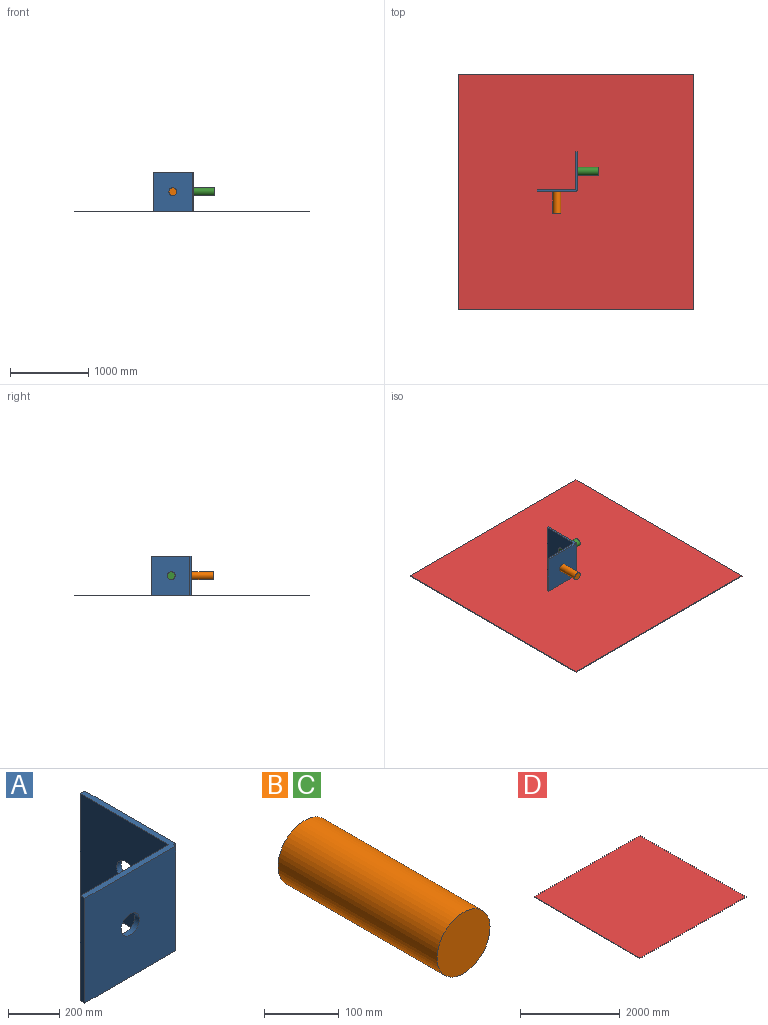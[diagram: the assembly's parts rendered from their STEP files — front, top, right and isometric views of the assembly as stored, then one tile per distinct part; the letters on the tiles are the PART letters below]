
ASSEMBLY  parts=4 mates=3
PART A: 12 faces, bbox 512.5x512.5x500 mm
  f0: plane 500x487.5mm, normal (0,1,0), area 235896mm2, adj f1,f3,f4,f5,f8
  f1: plane 512.5x512.5mm, normal (0,0,-1), area 24843.8mm2, adj f0,f2,f5,f6,f7,f8,f9,f11
  f2: plane 500x12.5mm, normal (1,0,0), area 6250mm2, adj f1,f3,f6,f7
  f3: plane 512.5x512.5mm, normal (0,0,1), area 24843.8mm2, adj f0,f2,f5,f6,f7,f8,f9,f11
  f4: cylinder r=50mm len=100mm, axis (0,1,0), area 7854mm2, adj f0,f6
  f5: plane 500x25mm, normal (-1,0,0), area 12500mm2, adj f0,f1,f3,f6
  f6: plane 500x500mm, normal (0,-1,0), area 242146mm2, adj f1,f2,f3,f4,f5
  f7: plane 500x12.5mm, normal (0,-1,0), area 6250mm2, adj f1,f2,f3,f11
  f8: plane 500x487.5mm, normal (-1,0,0), area 235896mm2, adj f0,f1,f3,f9,f10
  f9: plane 500x25mm, normal (0,1,0), area 12500mm2, adj f1,f3,f8,f11
  f10: cylinder r=50mm len=100mm, axis (-1,0,0), area 7854mm2, adj f8,f11
  f11: plane 500x500mm, normal (1,0,0), area 242146mm2, adj f1,f3,f7,f9,f10
PART B: 3 faces, bbox 100x300x100 mm
  f0: cylinder r=50mm len=300mm, axis (0,1,0), area 94247.8mm2, adj f1,f2
  f1: plane 100x100mm, normal (0,-1,0), area 7854mm2, adj f0
  f2: plane 100x100mm, normal (0,1,0), area 7854mm2, adj f0
PART C: same geometry as B
PART D: 6 faces, bbox 3000x3000x10 mm
  f0: plane 3000x10mm, normal (0,1,0), area 30000mm2, adj f1,f3,f4,f5
  f1: plane 3000x10mm, normal (-1,0,0), area 30000mm2, adj f0,f2,f4,f5
  f2: plane 3000x10mm, normal (0,-1,0), area 30000mm2, adj f1,f3,f4,f5
  f3: plane 3000x10mm, normal (1,0,0), area 30000mm2, adj f0,f2,f4,f5
  f4: plane 3000x3000mm, normal (0,0,1), area 9000000mm2, adj f0,f1,f2,f3
  f5: plane 3000x3000mm, normal (0,0,-1), area 9000000mm2, adj f0,f1,f2,f3
PLACE A rot(axis=(0.2,-0.56,-0.8),0deg) t=(4.22,15.32,-0.92)mm
PLACE B rot(axis=(0.2,-0.56,-0.8),0deg) t=(-1307.7,27.82,-54.82)mm
PLACE C rot(axis=(0,0,1),90deg) t=(-8.28,-796.6,-54.82)mm
PLACE D rot(axis=(0.34,-0.94,0),0deg) t=(0,0,-10.92)mm
MATE revolute C.f0 <-> A.f10  axis (-1,0,0) through (-8.28,265.32,249.08)mm
MATE planar A.f1 <-> D.f4  axis (0,0,1) through (4.22,15.32,-0.92)mm
MATE revolute B.f0 <-> A.f4  axis (0,1,0) through (-245.78,27.82,249.08)mm
